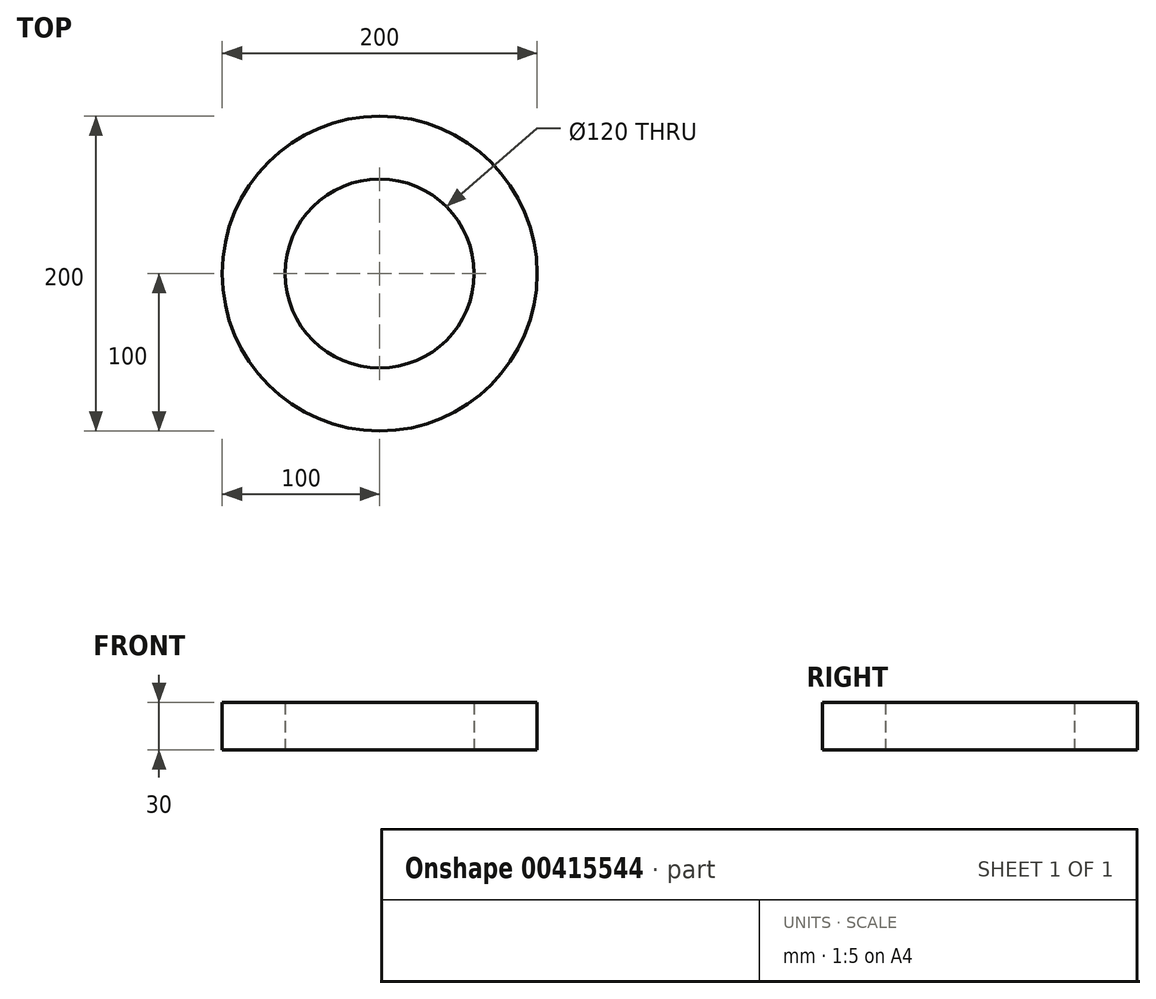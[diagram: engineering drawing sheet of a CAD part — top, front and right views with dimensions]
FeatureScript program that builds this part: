
annotation { "Feature Type Name" : "Feature", "Feature Type Description" : "" }
export const myFeature = defineFeature(function(context is Context, id is Id, definition is map)
    precondition{}
    {
        {
            var Q0;
            Q0=qCreatedBy(makeId("Front.planeOp"),FACE);
            var sketch = newSketch(context, id + "F0", { "sketchPlane" : qUnion([Q0])});
            skLineSegment(sketch, "E0", {"start": v(-80, 22.36) * mm, "end": v(-80, -23.08) * mm, "construction": true});
            skLineSegment(sketch, "E1", {"start": v(-100, 15) * mm, "end": v(-60, 15) * mm});
            skLineSegment(sketch, "E2", {"start": v(-60, 15) * mm, "end": v(-60, -15) * mm});
            skLineSegment(sketch, "E3", {"start": v(-60, -15) * mm, "end": v(-100, -15) * mm});
            skLineSegment(sketch, "E4", {"start": v(-100, -15) * mm, "end": v(-100, 15) * mm});
            skLineSegment(sketch, "E5", {"start": v(0, -102.53) * mm, "end": v(0, 103.53) * mm});
            skSolve(sketch);
        }
        {
            var Q0;
            Q0=makeQuery(id+"F0.imprint","IMPRINT",FACE,{"disambiguationData":[TD([[makeQuery(id+"F0.imprint","IMPRINT",EDGE,{"derivedFrom":sQuery(id+"F0.wireOp",EDGE,"E1")}),-1.0]])]});
            var Q1;
            Q1=sQuery(id+"F0.wireOp",EDGE,"E5");
            revolve(context, id + "F1", {"entities" : qUnion([Q0]), "axis" : qUnion([Q1]), "revolveType" : RevolveType.FULL});
        }
    });
